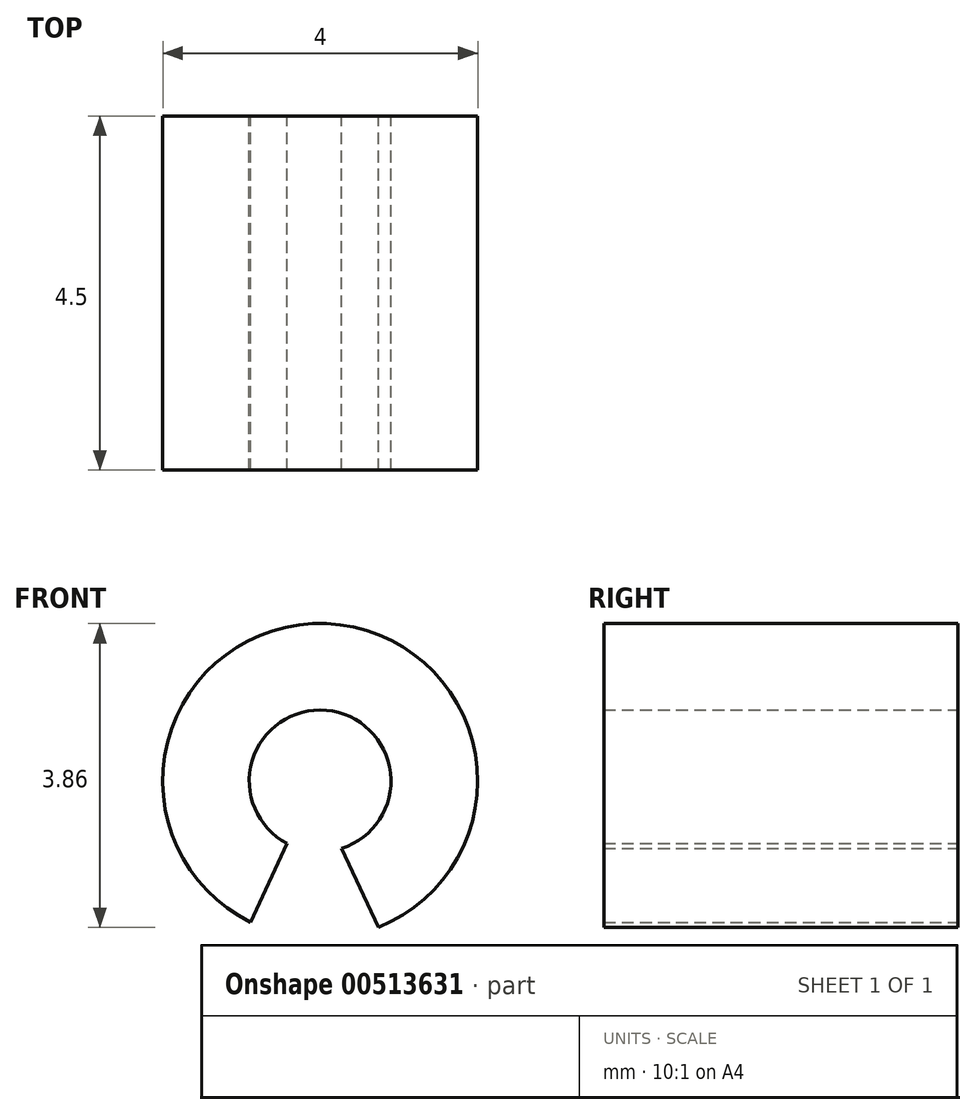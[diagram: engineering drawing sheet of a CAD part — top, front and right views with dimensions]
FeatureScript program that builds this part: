
annotation { "Feature Type Name" : "Feature", "Feature Type Description" : "" }
export const myFeature = defineFeature(function(context is Context, id is Id, definition is map)
    precondition{}
    {
        {
            var Q0;
            Q0=qCreatedBy(makeId("Front.planeOp"),FACE);
            var sketch = newSketch(context, id + "F0", { "sketchPlane" : qUnion([Q0])});
            skArc(sketch, "E0", {"start": v(-8.93, 4.47) * mm, "mid": v(-9.6, 8.33) * mm, "end": v(-10.56, 4.54) * mm});
            skArc(sketch, "E1", {"start": v(-9.4, 5.48) * mm, "mid": v(-9.6, 7.23) * mm, "end": v(-10.1, 5.54) * mm});
            skLineSegment(sketch, "E2", {"start": v(-9.67, 5.43) * mm, "end": v(-9.67, 2.77) * mm, "construction": true});
            skLineSegment(sketch, "E3", {"start": v(-9.4, 5.48) * mm, "end": v(-8.93, 4.47) * mm});
            skLineSegment(sketch, "E4", {"start": v(-10.1, 5.54) * mm, "end": v(-10.56, 4.54) * mm});
            skSolve(sketch);
        }
        {
            var Q0;
            Q0 = qSketchRegion(id + "F0", true);
            extrude(context, id + "F1", {"entities" : qUnion([Q0]), "depth" : 4.5 * mm, "offsetDistance" : 25 * mm});
        }
    });
